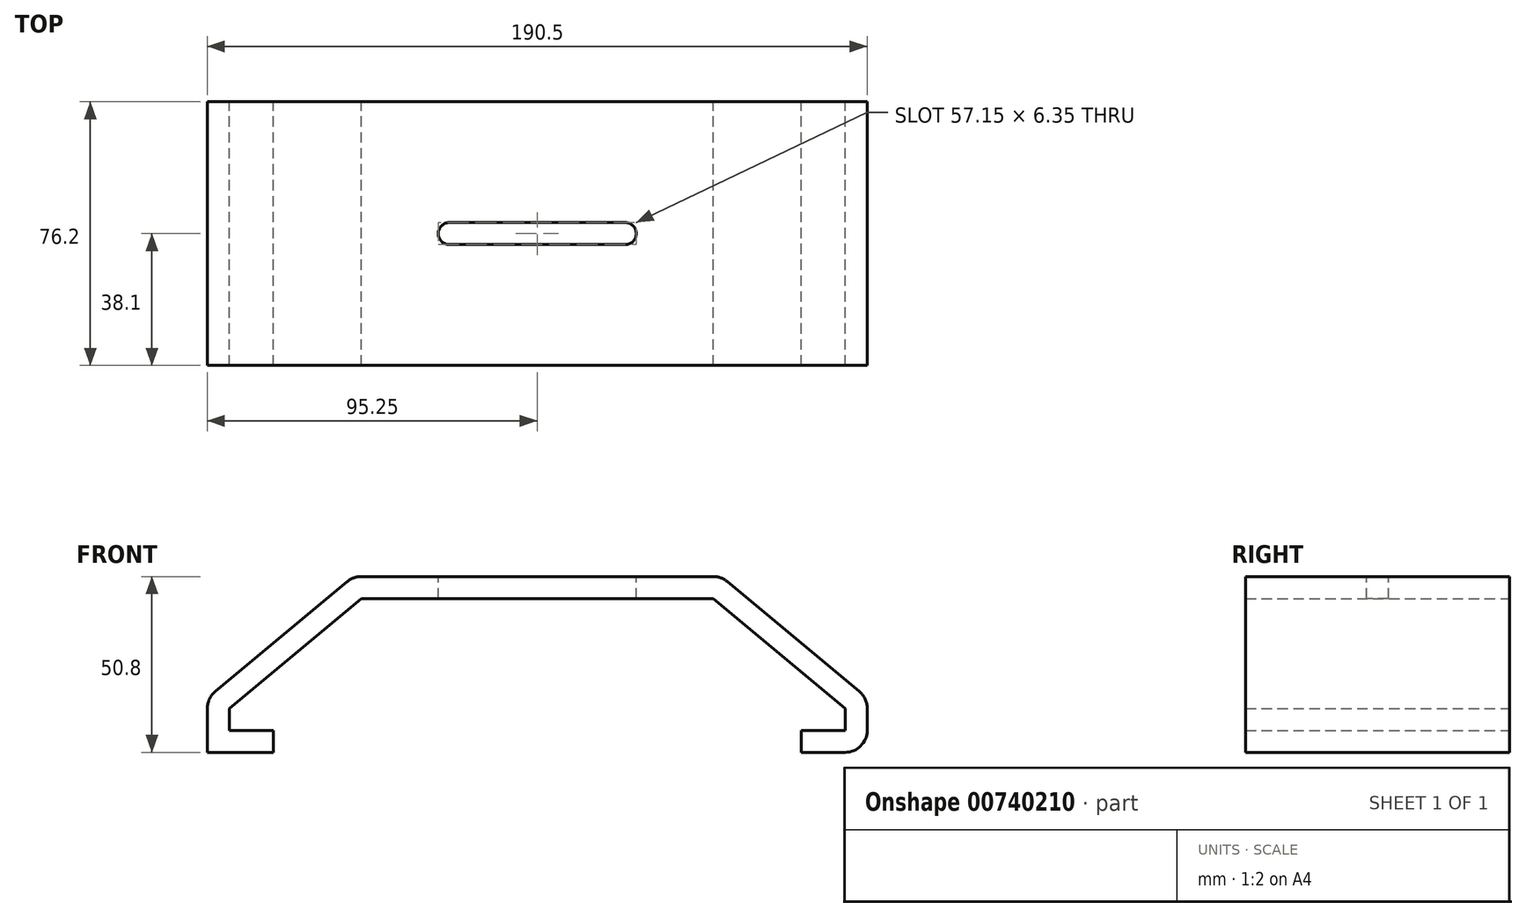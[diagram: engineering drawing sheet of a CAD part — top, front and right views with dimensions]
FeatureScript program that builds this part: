
annotation { "Feature Type Name" : "Feature", "Feature Type Description" : "" }
export const myFeature = defineFeature(function(context is Context, id is Id, definition is map)
    precondition{}
    {
        {
            var Q0;
            Q0=qCreatedBy(makeId("Front.planeOp"),FACE);
            var sketch = newSketch(context, id + "F0", { "sketchPlane" : qUnion([Q0])});
            skLineSegment(sketch, "E0", {"start": v(76.2, -5.74) * mm, "end": v(88.9, -5.74) * mm});
            skLineSegment(sketch, "E1", {"start": v(88.9, -5.74) * mm, "end": v(88.9, 0.6) * mm});
            skLineSegment(sketch, "E2", {"start": v(88.9, 0.6) * mm, "end": v(50.8, 32.36) * mm});
            skLineSegment(sketch, "E3", {"start": v(50.8, 32.36) * mm, "end": v(-50.8, 32.36) * mm});
            skLineSegment(sketch, "E4", {"start": v(-50.8, 32.36) * mm, "end": v(-88.9, 0.6) * mm});
            skLineSegment(sketch, "E5", {"start": v(-88.9, 0.6) * mm, "end": v(-88.9, -5.74) * mm});
            skLineSegment(sketch, "E6", {"start": v(-88.9, -5.74) * mm, "end": v(-76.2, -5.74) * mm});
            skPoint(sketch, "E7", {"position": v(0, 32.36) * mm});
            skLineSegment(sketch, "E8.0", {"start": v(-53.1, 38.7) * mm, "end": v(-95.25, 3.58) * mm});
            skLineSegment(sketch, "E8.1", {"start": v(53.1, 38.7) * mm, "end": v(-53.1, 38.7) * mm});
            skLineSegment(sketch, "E8.2", {"start": v(76.2, -5.74) * mm, "end": v(76.2, -12.1) * mm});
            skLineSegment(sketch, "E8.3", {"start": v(76.2, -12.1) * mm, "end": v(95.25, -12.1) * mm});
            skLineSegment(sketch, "E8.4", {"start": v(95.25, -12.1) * mm, "end": v(95.25, 3.58) * mm});
            skLineSegment(sketch, "E8.5", {"start": v(95.25, 3.58) * mm, "end": v(53.1, 38.7) * mm});
            skLineSegment(sketch, "E9.0", {"start": v(-76.2, -12.1) * mm, "end": v(-76.2, -5.74) * mm});
            skLineSegment(sketch, "E10.0", {"start": v(-95.25, -12.1) * mm, "end": v(-76.2, -12.1) * mm});
            skLineSegment(sketch, "E10.1", {"start": v(-95.25, 3.58) * mm, "end": v(-95.25, -12.1) * mm});
            skSolve(sketch);
        }
        {
            var Q0;
            Q0 = qSketchRegion(id + "F0", true);
            extrude(context, id + "F1", {"entities" : qUnion([Q0]), "depth" : 76.2 * mm, "offsetDistance" : 25.4 * mm});
        }
        {
            var Q0;
            Q0=makeQuery(id+"F1.opExtrude","SWEPT_EDGE",EDGE,{"disambiguationData":[OSD([sQuery(id+"F0.wireOp",EDGE,"E8.0"),sQuery(id+"F0.wireOp",EDGE,"E8.1")])]});
            var Q1;
            Q1=makeQuery(id+"F1.opExtrude","SWEPT_EDGE",EDGE,{"disambiguationData":[OSD([sQuery(id+"F0.wireOp",EDGE,"E8.1"),sQuery(id+"F0.wireOp",EDGE,"E8.5")])]});
            var Q2;
            Q2=makeQuery(id+"F1.opExtrude","SWEPT_EDGE",EDGE,{"disambiguationData":[OSD([sQuery(id+"F0.wireOp",EDGE,"E8.4"),sQuery(id+"F0.wireOp",EDGE,"E8.5")])]});
            var Q3;
            Q3=makeQuery(id+"F1.opExtrude","SWEPT_EDGE",EDGE,{"disambiguationData":[OSD([sQuery(id+"F0.wireOp",EDGE,"E8.3"),sQuery(id+"F0.wireOp",EDGE,"E8.4")])]});
            var Q4;
            Q4=makeQuery(id+"F1.opExtrude","SWEPT_EDGE",EDGE,{"disambiguationData":[OSD([sQuery(id+"F0.wireOp",EDGE,"E8.0"),sQuery(id+"F0.wireOp",EDGE,"E10.1")])]});
            fillet(context, id + "F2", {"entities" : qUnion([Q0, Q1, Q2, Q3, Q4]), "radius" : 6.35 * mm, "tangentPropagation" : true, "allowEdgeOverflow" : false});
        }
        {
            var Q0;
            Q0=makeQuery(id+"F1.opExtrude","SWEPT_FACE",FACE,{"disambiguationData":[OSD([sQuery(id+"F0.wireOp",EDGE,"E8.1")])]});
            var sketch = newSketch(context, id + "F3", { "sketchPlane" : qUnion([Q0])});
            skLineSegment(sketch, "E11", {"start": v(-25.4, -34.92) * mm, "end": v(25.4, -34.92) * mm});
            skPoint(sketch, "E12", {"position": v(0, -34.92) * mm});
            skLineSegment(sketch, "E13", {"start": v(-25.4, -41.27) * mm, "end": v(25.4, -41.27) * mm});
            skArc(sketch, "E14", {"start": v(-25.4, -34.92) * mm, "mid": v(-28.57, -38.1) * mm, "end": v(-25.4, -41.27) * mm});
            skArc(sketch, "E15", {"start": v(25.4, -41.28) * mm, "mid": v(28.57, -38.1) * mm, "end": v(25.4, -34.92) * mm});
            skSolve(sketch);
        }
        {
            var Q0;
            Q0 = qSketchRegion(id + "F3", true);
            extrude(context, id + "F4", {"entities" : qUnion([Q0]), "operationType" : NewBodyOperationType.REMOVE, "endBound" : BoundingType.THROUGH_ALL, "oppositeDirection" : true, "depth" : 25.4 * mm, "offsetDistance" : 25.4 * mm});
        }
    });
